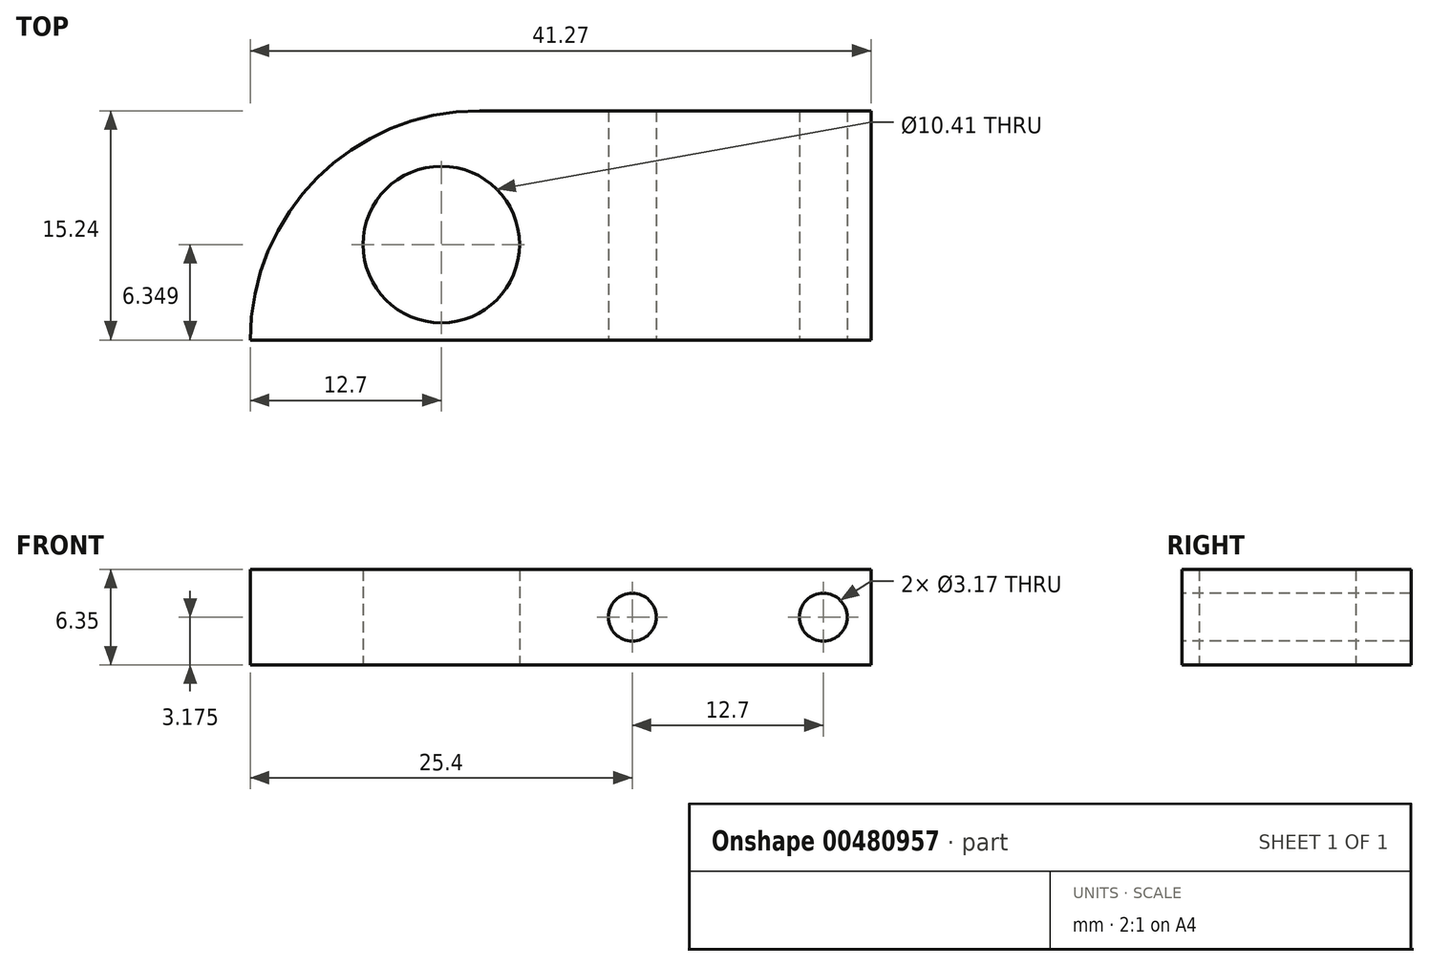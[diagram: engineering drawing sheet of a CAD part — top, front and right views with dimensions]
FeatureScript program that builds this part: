
annotation { "Feature Type Name" : "Feature", "Feature Type Description" : "" }
export const myFeature = defineFeature(function(context is Context, id is Id, definition is map)
    precondition{}
    {
        {
            var Q0;
            Q0=qCreatedBy(makeId("Top.planeOp"),FACE);
            var sketch = newSketch(context, id + "F0", { "sketchPlane" : qUnion([Q0])});
            skLineSegment(sketch, "E0.bottom", {"start": v(0, 0) * mm, "end": v(107.95, 0) * mm});
            skLineSegment(sketch, "E0.top", {"start": v(0, 15.24) * mm, "end": v(107.95, 15.24) * mm});
            skLineSegment(sketch, "E0.left", {"start": v(0, 0) * mm, "end": v(0, 15.24) * mm});
            skLineSegment(sketch, "E0.right", {"start": v(107.95, 0) * mm, "end": v(107.95, 15.24) * mm});
            skCircle(sketch, "E1", {"center": v(15.24, 0) * mm, "radius": 15.24 * mm});
            skCircle(sketch, "E2", {"center": v(92.7, 0) * mm, "radius": 15.24 * mm});
            skCircle(sketch, "E3", {"center": v(12.7, 6.35) * mm, "radius": 5.2 * mm});
            skCircle(sketch, "E4", {"center": v(95.25, 6.35) * mm, "radius": 5.2 * mm});
            skLineSegment(sketch, "E5", {"start": v(41.28, 15.24) * mm, "end": v(41.28, 0) * mm});
            skPoint(sketch, "E6", {"position": v(53.97, 0) * mm});
            skSolve(sketch);
        }
        {
            var Q0;
            {var subQ0=sQuery(id+"F0.wireOp",EDGE,"E1");var subQ1=sQuery(id+"F0.wireOp",EDGE,"E0.bottom");var subQ2=makeQuery(id+"F0.imprint","INTERSECT",VERTEX,{"derivedFrom":[subQ1,subQ0]});Q0=makeQuery(id+"F0.imprint","IMPRINT",FACE,{"disambiguationData":[TD([[makeQuery(id+"F0.imprint","IMPRINT",EDGE,{"disambiguationData":[TD([[subQ2,-1.0]])],"derivedFrom":subQ1}),1.0]])]});}
            var Q1;
            Q1=makeQuery(id+"F0.imprint","IMPRINT",FACE,{"disambiguationData":[TD([[makeQuery(id+"F0.imprint","IMPRINT",EDGE,{"derivedFrom":sQuery(id+"F0.wireOp",EDGE,"E3")}),-1.0]])]});
            extrude(context, id + "F1", {"entities" : qUnion([Q0, Q1]), "depth" : 6.35 * mm});
        }
        {
            var Q0;
            Q0=makeQuery(id+"F1.opExtrude","SWEPT_FACE",FACE,{"disambiguationData":[OSD([sQuery(id+"F0.wireOp",EDGE,"E0.bottom")])]});
            var sketch = newSketch(context, id + "F2", { "sketchPlane" : qUnion([Q0])});
            skPoint(sketch, "E7", {"position": v(25.4, 3.18) * mm});
            skPoint(sketch, "E8", {"position": v(38.1, 3.18) * mm});
            skSolve(sketch);
        }
        {
            var Q0;
            Q0=sQuery(id+"F2.wireOp",VERTEX,"E7");
            var Q1;
            Q1=sQuery(id+"F2.wireOp",VERTEX,"E8");
            var Q2;
            Q2=makeQuery(id+"F1.opExtrude","SWEPT_BODY",BODY,{"disambiguationData":[OSD([sQuery(id+"F0.wireOp",EDGE,"E0.bottom"),sQuery(id+"F0.wireOp",EDGE,"E0.top"),sQuery(id+"F0.wireOp",EDGE,"E1"),sQuery(id+"F0.wireOp",EDGE,"E3"),sQuery(id+"F0.wireOp",EDGE,"E5")])]});
            hole(context, id + "F3", {"style" : HoleStyle.SIMPLE, "endStyle" : HoleEndStyle.THROUGH, "holeDiameter" : 3.17 * mm, "isTappedThrough" : true, "tappedDepth" : 12.7 * mm, "tapClearance" : 3, "locations" : qUnion([Q0, Q1]), "scope" : qUnion([Q2])});
        }
    });
